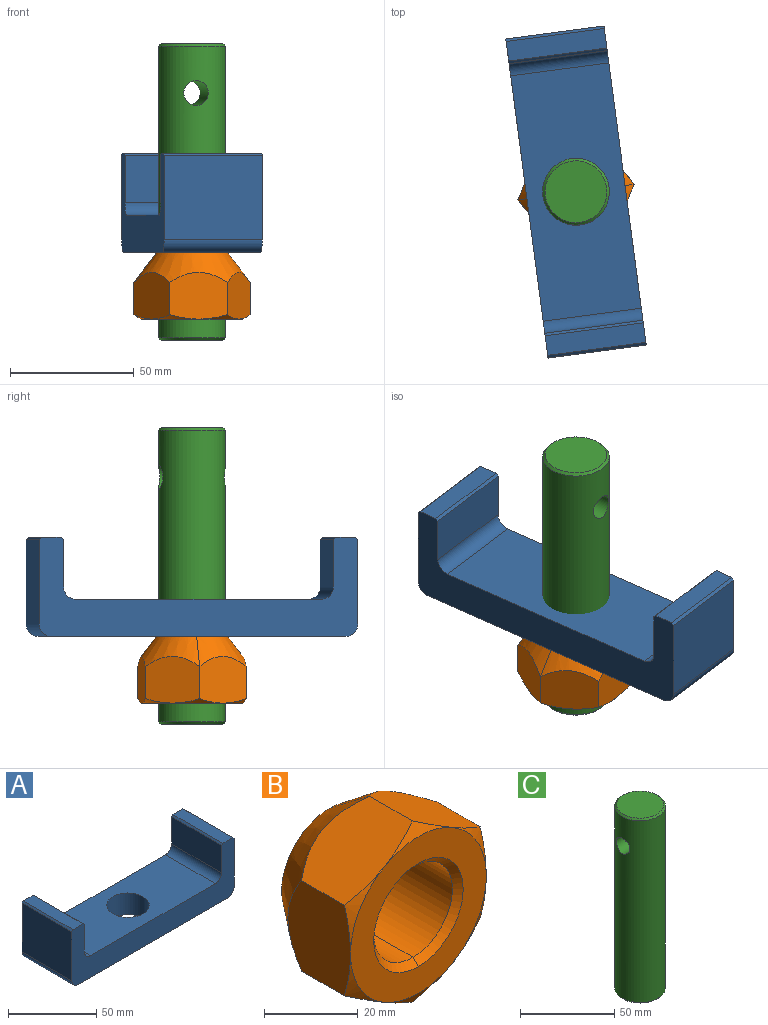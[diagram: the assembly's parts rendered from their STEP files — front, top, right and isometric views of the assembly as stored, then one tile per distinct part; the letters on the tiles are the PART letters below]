
ASSEMBLY  parts=3 mates=3
PART A: 19 faces, bbox 130x40x40 mm
  f0: plane 40x8mm, normal (0,0,1), area 320mm2, adj f5,f6,f15,f16
  f1: plane 40x8mm, normal (0,0,1), area 320mm2, adj f5,f6,f17,f18
  f2: plane 40x34mm, normal (-1,0,0), area 1360mm2, adj f5,f6,f11,f18
  f3: plane 120x40mm, normal (0,0,-1), area 4347.6mm2, adj f5,f6,f10,f11,f12
  f4: plane 40x34mm, normal (1,0,0), area 1360mm2, adj f5,f6,f12,f15
  f5: plane 130x40mm, normal (0,-1,0), area 2448mm2, adj f0,f1,f2,f3,f4,f7,f8,f9
  f6: plane 130x40mm, normal (0,1,0), area 2448mm2, adj f0,f1,f2,f3,f4,f7,f8,f9
  f7: plane 40x19mm, normal (1,0,0), area 760mm2, adj f5,f6,f13,f17
  f8: plane 100x40mm, normal (0,0,1), area 3547.6mm2, adj f5,f6,f10,f13,f14
  f9: plane 40x19mm, normal (-1,0,0), area 760mm2, adj f5,f6,f14,f16
  f10: cylinder r=12mm len=24mm, axis (0,0,-1), area 1131mm2, adj f3,f8
  f11: cylinder r=5mm len=40mm, axis (0,1,0), area 314.2mm2, adj f2,f3,f5,f6
  f12: cylinder r=5mm len=40mm, axis (0,-1,0), area 314.2mm2, adj f3,f4,f5,f6
  f13: cylinder r=5mm len=40mm, axis (0,1,0), area 314.2mm2, adj f5,f6,f7,f8
  f14: cylinder r=5mm len=40mm, axis (0,-1,0), area 314.2mm2, adj f5,f6,f8,f9
  f15: plane 40x1mm, normal (0.71,0,0.71), area 56.6mm2, adj f0,f4,f5,f6
  f16: plane 40x1mm, normal (-0.71,0,0.71), area 56.6mm2, adj f0,f5,f6,f9
  f17: plane 40x1mm, normal (0.71,0,0.71), area 56.6mm2, adj f1,f5,f6,f7
  f18: plane 40x1mm, normal (-0.71,0,0.71), area 56.6mm2, adj f1,f2,f5,f6
PART B: 22 faces, bbox 47.3x27x47.3 mm
  f0: plane 20.5x18.93mm, normal (-0.5,0,-0.87), area 399.7mm2, adj f1,f5,f6,f16,f17
  f1: plane 20.5x18.93mm, normal (0.5,0,-0.87), area 399.7mm2, adj f0,f2,f7,f16,f21
  f2: plane 23.67x18.93mm, normal (1,0,0), area 399.7mm2, adj f1,f3,f7,f20,f21
  f3: plane 20.5x18.93mm, normal (0.5,0,0.87), area 399.7mm2, adj f2,f4,f7,f19,f20
  f4: plane 20.5x18.93mm, normal (-0.5,0,0.87), area 399.7mm2, adj f3,f5,f6,f18,f19
  f5: plane 23.67x18.93mm, normal (-1,0,0), area 399.7mm2, adj f0,f4,f6,f17,f18
  f6: cone r=30.57mm half-angle=37.5deg, axis (0,-1,0), area 667.6mm2, adj f0,f4,f5,f7,f8
  f7: cone r=30.57mm half-angle=37.5deg, axis (0,-1,0), area 667.6mm2, adj f1,f2,f3,f6,f8
  f8: plane 28.6x28.6mm, normal (0,1,0), area 69.9mm2, adj f6,f7,f9,f10
  f9: cone r=13.5mm half-angle=45deg, axis (0,1,0), area 91.5mm2, adj f8,f10,f12
  f10: cone r=13.5mm half-angle=45deg, axis (0,1,0), area 91.5mm2, adj f8,f9,f11
  f11: cylinder r=11.88mm len=23.75mm, axis (0,1,0), area 886.2mm2, adj f10,f12,f14
  f12: cylinder r=11.88mm len=23.75mm, axis (0,1,0), area 886.2mm2, adj f9,f11,f13
  f13: cone r=11.88mm half-angle=45deg, axis (0,-1,0), area 91.5mm2, adj f12,f14,f15
  f14: cone r=11.88mm half-angle=45deg, axis (0,-1,0), area 91.5mm2, adj f11,f13,f15
  f15: plane 41x41mm, normal (0,-1,0), area 747.7mm2, adj f13,f14,f16,f17,f18,f19,f20,f21
  f16: cone r=20.5mm half-angle=60deg, axis (0,1,0), area 26.1mm2, adj f0,f1,f15
  f17: cone r=20.5mm half-angle=60deg, axis (0,1,0), area 26.1mm2, adj f0,f5,f15
  f18: cone r=20.5mm half-angle=60deg, axis (0,1,0), area 26.1mm2, adj f4,f5,f15
  f19: cone r=20.5mm half-angle=60deg, axis (0,1,0), area 26.1mm2, adj f3,f4,f15
  f20: cone r=20.5mm half-angle=60deg, axis (0,1,0), area 26.1mm2, adj f2,f3,f15
  f21: cone r=20.5mm half-angle=60deg, axis (0,1,0), area 26.1mm2, adj f1,f2,f15
PART C: 6 faces, bbox 27x27x120 mm
  f0: cylinder r=13.5mm len=118mm, axis (0,0,-1), area 9849.2mm2, adj f3,f4,f5
  f1: plane 25x25mm, normal (0,0,1), area 490.9mm2, adj f5
  f2: plane 25x25mm, normal (0,0,-1), area 490.9mm2, adj f4
  f3: cylinder r=5mm len=27mm, axis (1,0,0), area 818.3mm2, adj f0
  f4: cone r=13.5mm half-angle=45deg, axis (0,0,1), area 115.5mm2, adj f0,f2
  f5: cone r=12.5mm half-angle=45deg, axis (0,0,-1), area 115.5mm2, adj f0,f1
PLACE A rot(axis=(0,0,-1),82.4deg) t=(41.38,23.63,15.29)mm
PLACE B rot(axis=(0.63,-0.55,-0.55),115.7deg) t=(41.38,23.63,-31.71)mm
PLACE C rot(axis=(0,0,-1),82.4deg) t=(41.38,23.63,19.69)mm
MATE slider B.f6 <-> C.f0  axis (0,0,1) through (41.38,23.63,-30.08)mm
MATE slider A.f10 <-> C.f0  axis (0,0,1) through (41.38,23.63,10.29)mm
MATE planar B.f6 <-> A.f10  axis (0,0,1) through (41.38,23.63,-4.71)mm
